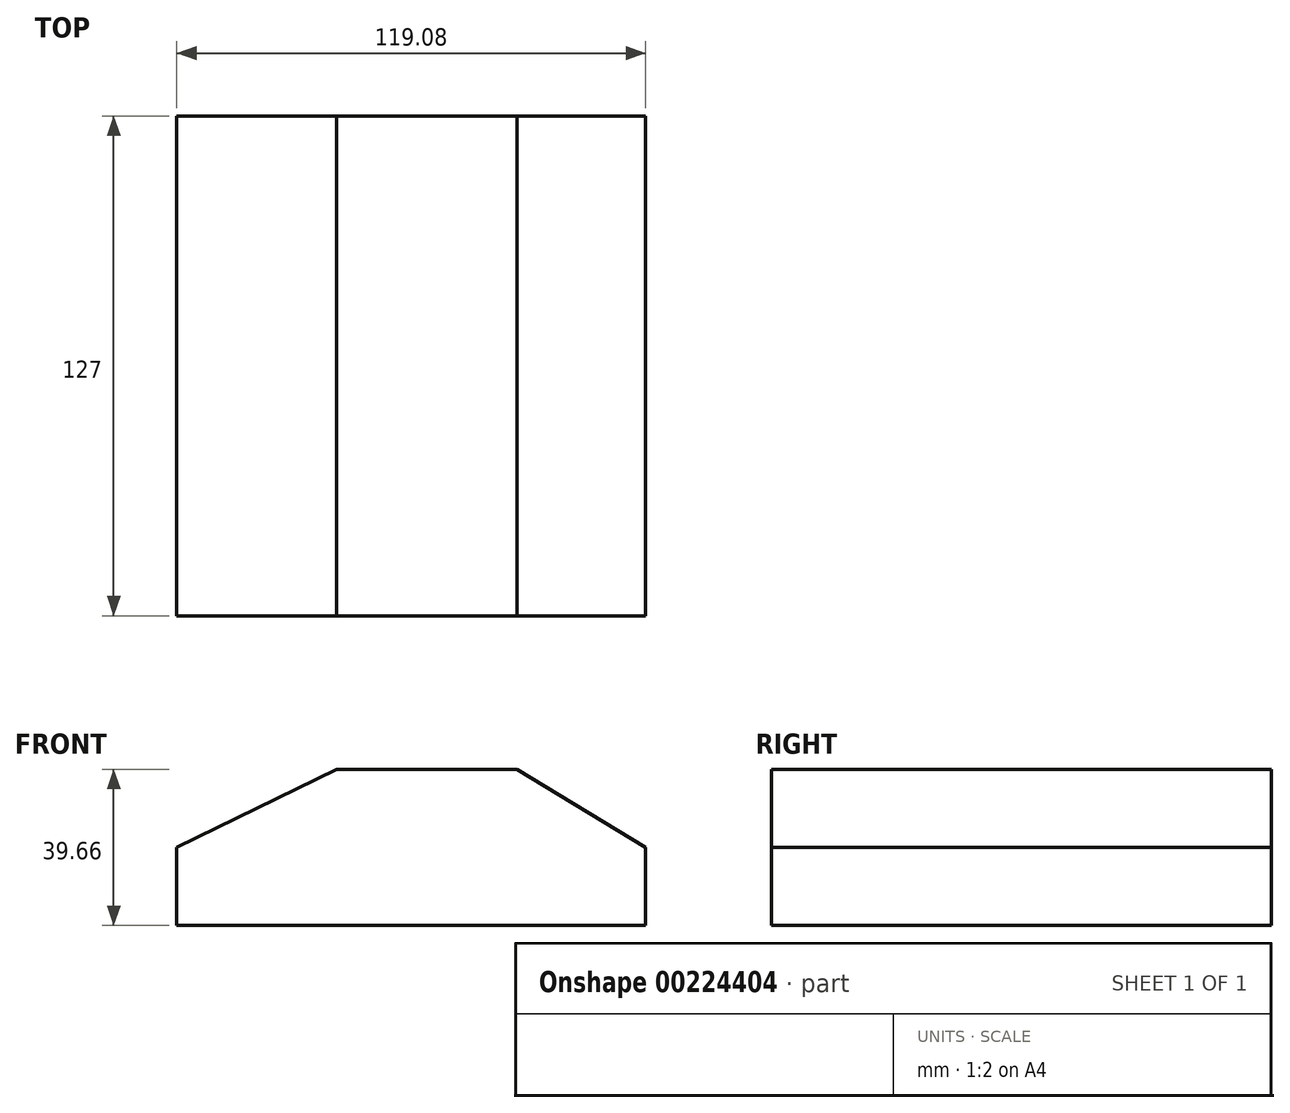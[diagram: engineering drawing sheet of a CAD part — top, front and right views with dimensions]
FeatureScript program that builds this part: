
annotation { "Feature Type Name" : "Feature", "Feature Type Description" : "" }
export const myFeature = defineFeature(function(context is Context, id is Id, definition is map)
    precondition{}
    {
        {
            var Q0;
            Q0=qCreatedBy(makeId("Front.planeOp"),FACE);
            var sketch = newSketch(context, id + "F0", { "sketchPlane" : qUnion([Q0])});
            skLineSegment(sketch, "E0.bottom", {"start": v(-59.2, -5.44) * mm, "end": v(59.87, -5.44) * mm});
            skLineSegment(sketch, "E0.top", {"start": v(-59.2, 34.22) * mm, "end": v(59.87, 34.22) * mm});
            skLineSegment(sketch, "E0.left", {"start": v(-59.2, -5.44) * mm, "end": v(-59.2, 34.22) * mm});
            skLineSegment(sketch, "E0.right", {"start": v(59.87, -5.44) * mm, "end": v(59.87, 34.22) * mm});
            skLineSegment(sketch, "E1", {"start": v(-59.2, 14.39) * mm, "end": v(-18.59, 34.22) * mm});
            skLineSegment(sketch, "E2", {"start": v(27.28, 34.22) * mm, "end": v(59.87, 14.39) * mm});
            skSolve(sketch);
        }
        {
            var Q0;
            {var subQ1=sQuery(id+"F0.wireOp",EDGE,"E0.bottom");Q0=makeQuery(id+"F0.imprint","IMPRINT",FACE,{"disambiguationData":[TD([[makeQuery(id+"F0.imprint","IMPRINT",EDGE,{"derivedFrom":subQ1}),1.0]])]});}
            extrude(context, id + "F1", {"entities" : qUnion([Q0]), "endBound" : BoundingType.SYMMETRIC, "depth" : 127 * mm});
        }
    });
